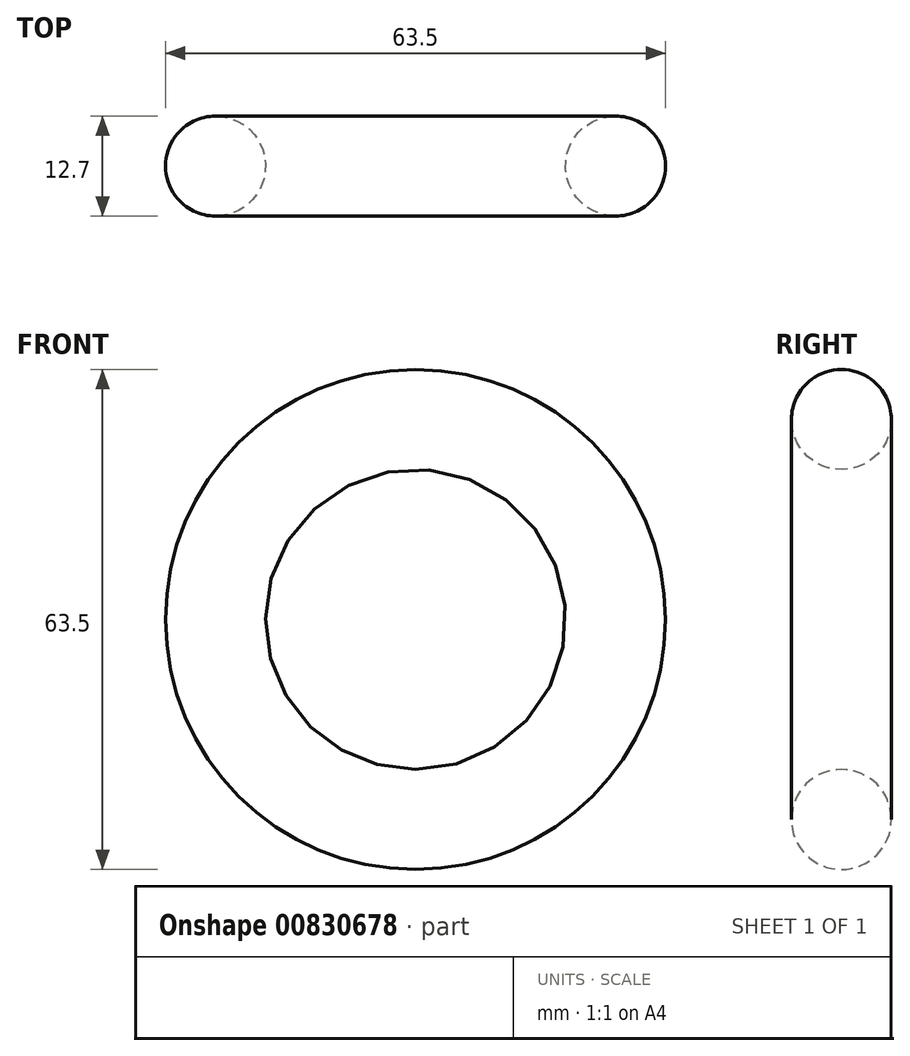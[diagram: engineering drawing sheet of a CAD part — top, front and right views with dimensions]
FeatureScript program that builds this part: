
annotation { "Feature Type Name" : "Feature", "Feature Type Description" : "" }
export const myFeature = defineFeature(function(context is Context, id is Id, definition is map)
    precondition{}
    {
        {
            var Q0;
            Q0=qCreatedBy(makeId("Top.planeOp"),FACE);
            var sketch = newSketch(context, id + "F0", { "sketchPlane" : qUnion([Q0])});
            skLineSegment(sketch, "E0", {"start": v(0, 0) * mm, "end": v(25.4, 0) * mm, "construction": true});
            skLineSegment(sketch, "E1", {"start": v(0, 0) * mm, "end": v(0, 12.7) * mm, "construction": true});
            skLineSegment(sketch, "E2", {"start": v(0, 0) * mm, "end": v(0, -12.7) * mm, "construction": true});
            skCircle(sketch, "E3", {"center": v(25.4, 0) * mm, "radius": 6.35 * mm});
            skSolve(sketch);
        }
        {
            var Q0;
            Q0=makeQuery(id+"F0.imprint","IMPRINT",FACE,{"disambiguationData":[TD([[makeQuery(id+"F0.imprint","IMPRINT",EDGE,{"derivedFrom":sQuery(id+"F0.wireOp",EDGE,"E3")}),1.0]])]});
            var Q1;
            Q1=sQuery(id+"F0.wireOp",EDGE,"E1");
            revolve(context, id + "F1", {"surfaceOperationType" : NewSurfaceOperationType.NEW, "entities" : qUnion([Q0]), "axis" : qUnion([Q1]), "revolveType" : RevolveType.FULL});
        }
    });
